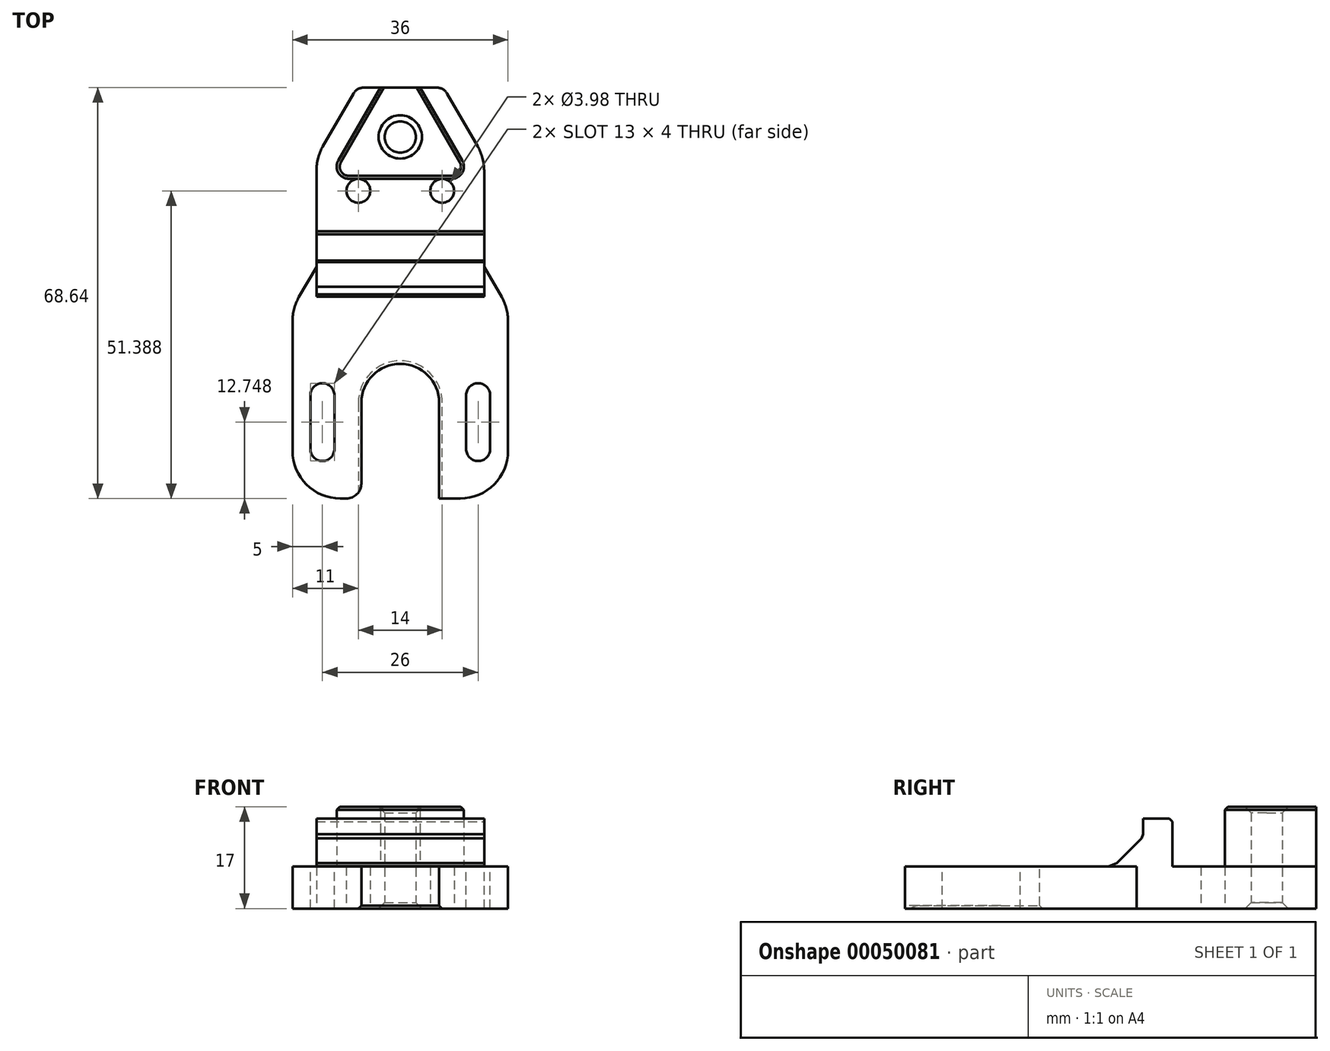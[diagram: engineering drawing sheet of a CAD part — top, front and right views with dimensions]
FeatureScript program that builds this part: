
annotation { "Feature Type Name" : "Feature", "Feature Type Description" : "" }
export const myFeature = defineFeature(function(context is Context, id is Id, definition is map)
    precondition{}
    {
        {
            var Q0;
            Q0=qCreatedBy(makeId("Top.planeOp"),FACE);
            var sketch = newSketch(context, id + "F0", { "sketchPlane" : qUnion([Q0])});
            skLineSegment(sketch, "E0", {"start": v(-12.34, -7.12) * mm, "end": v(0, 14.25) * mm});
            skLineSegment(sketch, "E1", {"start": v(0, 14.25) * mm, "end": v(12.34, -7.12) * mm});
            skLineSegment(sketch, "E2", {"start": v(12.34, -7.12) * mm, "end": v(-12.34, -7.12) * mm});
            skLineSegment(sketch, "E3", {"start": v(-12.34, -7.12) * mm, "end": v(6.17, 3.56) * mm, "construction": true});
            skPoint(sketch, "E3.endSnap0", {"position": v(6.17, 3.56) * mm});
            skLineSegment(sketch, "E4", {"start": v(12.34, -7.12) * mm, "end": v(-6.17, 3.56) * mm, "construction": true});
            skPoint(sketch, "E5", {"position": v(0, 0) * mm});
            skSolve(sketch);
        }
        {
            var Q0;
            Q0 = qSketchRegion(id + "F0", true);
            extrude(context, id + "F1", {"entities" : qUnion([Q0]), "depth" : 10 * mm, "offsetDistance" : 25 * mm});
        }
        {
            var Q0;
            Q0=makeQuery(id+"F1.opExtrude","CAP_FACE",FACE,{"disambiguationData":[OSD([sQuery(id+"F0.wireOp",EDGE,"E0"),sQuery(id+"F0.wireOp",EDGE,"E1"),sQuery(id+"F0.wireOp",EDGE,"E2")])],"isStart":true});
            var sketch = newSketch(context, id + "F2", { "sketchPlane" : qUnion([Q0])});
            skLineSegment(sketch, "E6", {"start": v(0, -20.78) * mm, "end": v(-18, 10.4) * mm});
            skLineSegment(sketch, "E7", {"start": v(-18, 10.4) * mm, "end": v(18, 10.4) * mm});
            skLineSegment(sketch, "E8", {"start": v(18, 10.4) * mm, "end": v(0, -20.78) * mm});
            skLineSegment(sketch, "E9", {"start": v(18, 10.4) * mm, "end": v(-9, -5.2) * mm, "construction": true});
            skLineSegment(sketch, "E10", {"start": v(0, -20.78) * mm, "end": v(0, 10.4) * mm, "construction": true});
            skLineSegment(sketch, "E11", {"start": v(-18, 10.4) * mm, "end": v(9, -5.2) * mm, "construction": true});
            skPoint(sketch, "E12", {"position": v(0, 0) * mm});
            skSolve(sketch);
        }
        {
            var Q0;
            Q0 = qSketchRegion(id + "F2", true);
            extrude(context, id + "F3", {"entities" : qUnion([Q0]), "operationType" : NewBodyOperationType.ADD, "depth" : 7 * mm, "offsetDistance" : 25 * mm});
        }
        {
            var Q0;
            Q0=qCreatedBy(makeId("Top.planeOp"),FACE);
            var sketch = newSketch(context, id + "F4", { "sketchPlane" : qUnion([Q0])});
            skLineSegment(sketch, "E13.0", {"start": v(-18, -10.4) * mm, "end": v(18, -10.4) * mm, "construction": true});
            skPoint(sketch, "E14.0", {"position": v(0, 14.25) * mm});
            skLineSegment(sketch, "E15", {"start": v(-11.46, 8.25) * mm, "end": v(13.33, 8.25) * mm});
            skLineSegment(sketch, "E16", {"start": v(13.33, 8.25) * mm, "end": v(13.33, 20.97) * mm});
            skLineSegment(sketch, "E17", {"start": v(13.33, 20.97) * mm, "end": v(-11.55, 20.97) * mm});
            skLineSegment(sketch, "E18", {"start": v(-11.55, 20.97) * mm, "end": v(-11.46, 8.25) * mm});
            skLineSegment(sketch, "E19.0", {"start": v(0, 20.78) * mm, "end": v(-18, -10.4) * mm, "construction": true});
            skLineSegment(sketch, "E20.0", {"start": v(18, -10.4) * mm, "end": v(0, 20.78) * mm, "construction": true});
            skLineSegment(sketch, "E21", {"start": v(-18, -10.4) * mm, "end": v(9, 5.2) * mm, "construction": true});
            skLineSegment(sketch, "E22", {"start": v(18, -10.4) * mm, "end": v(-9, 5.2) * mm, "construction": true});
            skPoint(sketch, "E23", {"position": v(0, 0) * mm});
            skCircle(sketch, "E24", {"center": v(0, 0) * mm, "radius": 2.62 * mm});
            skLineSegment(sketch, "E25.bottom", {"start": v(-19, -3) * mm, "end": v(-14, -3) * mm});
            skLineSegment(sketch, "E25.top", {"start": v(-19, -13) * mm, "end": v(-14, -13) * mm});
            skLineSegment(sketch, "E25.left", {"start": v(-19, -3) * mm, "end": v(-19, -13) * mm});
            skLineSegment(sketch, "E25.right", {"start": v(-14, -3) * mm, "end": v(-14, -13) * mm});
            skLineSegment(sketch, "E26.MirrorCS", {"start": v(19, -13) * mm, "end": v(14, -13) * mm});
            skLineSegment(sketch, "E27.MirrorCS", {"start": v(14, -3) * mm, "end": v(14, -13) * mm});
            skLineSegment(sketch, "E28.MirrorCS", {"start": v(19, -3) * mm, "end": v(19, -13) * mm});
            skLineSegment(sketch, "E29.MirrorCS", {"start": v(19, -3) * mm, "end": v(14, -3) * mm});
            skSolve(sketch);
        }
        {
            var Q0;
            Q0 = qSketchRegion(id + "F4", true);
            extrude(context, id + "F5", {"entities" : qUnion([Q0]), "operationType" : NewBodyOperationType.REMOVE, "endBound" : BoundingType.THROUGH_ALL, "depth" : 25 * mm, "hasSecondDirection" : true, "secondDirectionOppositeDirection" : true, "secondDirectionDepth" : 25 * mm, "offsetDistance" : 25 * mm});
        }
        {
            var Q0;
            Q0=makeQuery(id+"F3.opExtrude","SWEPT_FACE",FACE,{"disambiguationData":[OSD([sQuery(id+"F2.wireOp",EDGE,"E7")])]});
            var sketch = newSketch(context, id + "F6", { "sketchPlane" : qUnion([Q0])});
            skLineSegment(sketch, "E30.0", {"start": v(-14, -7) * mm, "end": v(-14, 0) * mm});
            skLineSegment(sketch, "E30.1", {"start": v(-14, -7) * mm, "end": v(14, -7) * mm});
            skLineSegment(sketch, "E30.2", {"start": v(14, -7) * mm, "end": v(14, 0) * mm});
            skLineSegment(sketch, "E30.3", {"start": v(-14, 0) * mm, "end": v(14, 0) * mm});
            skSolve(sketch);
        }
        {
            var Q0;
            Q0 = qSketchRegion(id + "F6", true);
            extrude(context, id + "F7", {"entities" : qUnion([Q0]), "operationType" : NewBodyOperationType.ADD, "depth" : 50 * mm, "offsetDistance" : 25 * mm});
        }
        {
            var Q0;
            Q0=makeQuery(id+"F7.boolean.opBoolean","MERGE",FACE,{"derivedFrom":[makeQuery(id+"F3.opExtrude","CAP_FACE",FACE,{"disambiguationData":[OSD([sQuery(id+"F2.wireOp",EDGE,"E6"),sQuery(id+"F2.wireOp",EDGE,"E7"),sQuery(id+"F2.wireOp",EDGE,"E8")])],"isStart":true}),makeQuery(id+"F7.opExtrude","SWEPT_FACE",FACE,{"disambiguationData":[OSD([sQuery(id+"F6.wireOp",EDGE,"E30.3")])]})]});
            var sketch = newSketch(context, id + "F8", { "sketchPlane" : qUnion([Q0])});
            skLineSegment(sketch, "E31.bottom", {"start": v(-14, -15.62) * mm, "end": v(14, -15.62) * mm});
            skLineSegment(sketch, "E31.top", {"start": v(-14, -20.62) * mm, "end": v(14, -20.62) * mm});
            skLineSegment(sketch, "E31.left", {"start": v(-14, -15.62) * mm, "end": v(-14, -20.62) * mm});
            skLineSegment(sketch, "E31.right", {"start": v(14, -15.62) * mm, "end": v(14, -20.62) * mm});
            skSolve(sketch);
        }
        {
            var Q0;
            Q0 = qSketchRegion(id + "F8", true);
            extrude(context, id + "F9", {"entities" : qUnion([Q0]), "operationType" : NewBodyOperationType.ADD, "depth" : 8 * mm});
        }
        {
            var Q0;
            Q0=makeQuery(id+"F9.opExtrude","CAP_EDGE",EDGE,{"disambiguationData":[OSD([sQuery(id+"F8.wireOp",EDGE,"E31.top")])],"isStart":true});
            chamfer(context, id + "F10", {"entities" : qUnion([Q0]), "width" : 5 * mm, "tangentPropagation" : true});
        }
        {
            var Q0;
            {var subQ1=sQuery(id+"F6.wireOp",EDGE,"E30.3");var subQ3=sQuery(id+"F8.wireOp",EDGE,"E31.top");Q0=makeQuery(id+"F10.opChamfer","BLEND_EDGE",EDGE,{"blendedFrom":[makeQuery(id+"F9.opExtrude","CAP_EDGE",EDGE,{"disambiguationData":[OSD([subQ3])],"isStart":true}),makeQuery(id+"F9.boolean.opBoolean","SPLIT",FACE,{"disambiguationData":[TD([makeQuery(id+"F9.opExtrude","SWEPT_FACE",FACE,{"disambiguationData":[OSD([subQ3])]})])],"derivedFrom":makeQuery(id+"F7.boolean.opBoolean","MERGE",FACE,{"derivedFrom":[makeQuery(id+"F3.opExtrude","CAP_FACE",FACE,{"disambiguationData":[OSD([sQuery(id+"F2.wireOp",EDGE,"E6"),sQuery(id+"F2.wireOp",EDGE,"E7"),sQuery(id+"F2.wireOp",EDGE,"E8")])],"isStart":true}),makeQuery(id+"F7.opExtrude","SWEPT_FACE",FACE,{"disambiguationData":[OSD([subQ1])]})]})})],"blendedInto":[makeQuery(id+"F9.boolean.opBoolean","SPLIT",FACE,{"disambiguationData":[TD([makeQuery(id+"F9.opExtrude","SWEPT_FACE",FACE,{"disambiguationData":[OSD([subQ3])]})])],"derivedFrom":makeQuery(id+"F7.boolean.opBoolean","MERGE",FACE,{"derivedFrom":[makeQuery(id+"F3.opExtrude","CAP_FACE",FACE,{"disambiguationData":[OSD([sQuery(id+"F2.wireOp",EDGE,"E6"),sQuery(id+"F2.wireOp",EDGE,"E7"),sQuery(id+"F2.wireOp",EDGE,"E8")])],"isStart":true}),makeQuery(id+"F7.opExtrude","SWEPT_FACE",FACE,{"disambiguationData":[OSD([subQ1])]})]})})]});}
            chamfer(context, id + "F11", {"entities" : qUnion([Q0]), "width" : 2 * mm, "tangentPropagation" : true});
        }
        {
            var Q0;
            {var subQ1=sQuery(id+"F6.wireOp",EDGE,"E30.3");var subQ3=sQuery(id+"F8.wireOp",EDGE,"E31.top");var subQ4=makeQuery(id+"F9.boolean.opBoolean","SPLIT",FACE,{"disambiguationData":[TD([makeQuery(id+"F9.opExtrude","SWEPT_FACE",FACE,{"disambiguationData":[OSD([subQ3])]})])],"derivedFrom":makeQuery(id+"F7.boolean.opBoolean","MERGE",FACE,{"derivedFrom":[makeQuery(id+"F3.opExtrude","CAP_FACE",FACE,{"disambiguationData":[OSD([sQuery(id+"F2.wireOp",EDGE,"E6"),sQuery(id+"F2.wireOp",EDGE,"E7"),sQuery(id+"F2.wireOp",EDGE,"E8")])],"isStart":true}),makeQuery(id+"F7.opExtrude","SWEPT_FACE",FACE,{"disambiguationData":[OSD([subQ1])]})]})});Q0=makeQuery(id+"F11.opChamfer","BLEND_EDGE",EDGE,{"blendedFrom":[makeQuery(id+"F10.opChamfer","BLEND_EDGE",EDGE,{"blendedFrom":[makeQuery(id+"F9.opExtrude","CAP_EDGE",EDGE,{"disambiguationData":[OSD([subQ3])],"isStart":true}),subQ4],"blendedInto":[subQ4]}),subQ4],"blendedInto":[subQ4]});}
            chamfer(context, id + "F12", {"entities" : qUnion([Q0]), "width" : 1 * mm, "tangentPropagation" : true});
        }
        {
            var Q0;
            {var subQ0=sQuery(id+"F8.wireOp",EDGE,"E31.top");Q0=makeQuery(id+"F10.opChamfer","BLEND_EDGE",EDGE,{"blendedFrom":[makeQuery(id+"F9.opExtrude","CAP_EDGE",EDGE,{"disambiguationData":[OSD([subQ0])],"isStart":true}),makeQuery(id+"F9.opExtrude","SWEPT_FACE",FACE,{"disambiguationData":[OSD([subQ0])]})],"blendedInto":[makeQuery(id+"F9.opExtrude","SWEPT_FACE",FACE,{"disambiguationData":[OSD([subQ0])]})]});}
            chamfer(context, id + "F13", {"entities" : qUnion([Q0]), "width" : 1 * mm, "tangentPropagation" : true});
        }
        {
            var Q0;
            Q0=makeQuery(id+"F5.boolean.opBoolean","INTERSECT",EDGE,{"derivedFrom":[makeQuery(id+"F3.opExtrude","SWEPT_FACE",FACE,{"disambiguationData":[OSD([sQuery(id+"F2.wireOp",EDGE,"E6")])]}),makeQuery(id+"F5.opExtrude","SWEPT_FACE",FACE,{"disambiguationData":[OSD([sQuery(id+"F4.wireOp",EDGE,"E25.right")])]})]});
            var Q1;
            Q1=makeQuery(id+"F5.boolean.opBoolean","INTERSECT",EDGE,{"derivedFrom":[makeQuery(id+"F3.opExtrude","SWEPT_FACE",FACE,{"disambiguationData":[OSD([sQuery(id+"F2.wireOp",EDGE,"E8")])]}),makeQuery(id+"F5.opExtrude","SWEPT_FACE",FACE,{"disambiguationData":[OSD([sQuery(id+"F4.wireOp",EDGE,"E27.MirrorCS")])]})]});
            fillet(context, id + "F14", {"entities" : qUnion([Q0, Q1]), "radius" : 8 * mm, "tangentPropagation" : true, "allowEdgeOverflow" : false});
        }
        {
            var Q0;
            Q0=makeQuery(id+"F5.boolean.opBoolean","INTERSECT",EDGE,{"derivedFrom":[makeQuery(id+"F1.opExtrude","CAP_FACE",FACE,{"disambiguationData":[OSD([sQuery(id+"F0.wireOp",EDGE,"E0"),sQuery(id+"F0.wireOp",EDGE,"E1"),sQuery(id+"F0.wireOp",EDGE,"E2")])],"isStart":false}),makeQuery(id+"F5.opExtrude","SWEPT_FACE",FACE,{"disambiguationData":[OSD([sQuery(id+"F4.wireOp",EDGE,"E24")])]})]});
            var Q1;
            Q1=makeQuery(id+"F5.boolean.opBoolean","INTERSECT",EDGE,{"derivedFrom":[makeQuery(id+"F3.opExtrude","CAP_FACE",FACE,{"disambiguationData":[OSD([sQuery(id+"F2.wireOp",EDGE,"E6"),sQuery(id+"F2.wireOp",EDGE,"E7"),sQuery(id+"F2.wireOp",EDGE,"E8")])],"isStart":false}),makeQuery(id+"F5.opExtrude","SWEPT_FACE",FACE,{"disambiguationData":[OSD([sQuery(id+"F4.wireOp",EDGE,"E24")])]})]});
            chamfer(context, id + "F15", {"entities" : qUnion([Q0, Q1]), "width" : 1 * mm, "tangentPropagation" : true});
        }
        {
            var Q0;
            {var subQ0=sQuery(id+"F2.wireOp",EDGE,"E8");var subQ1=sQuery(id+"F2.wireOp",EDGE,"E6");Q0=makeQuery(id+"F9.boolean.opBoolean","SPLIT",FACE,{"disambiguationData":[TD([makeQuery(id+"F1.opExtrude","SWEPT_FACE",FACE,{"disambiguationData":[OSD([sQuery(id+"F0.wireOp",EDGE,"E0")])]})])],"derivedFrom":makeQuery(id+"F7.boolean.opBoolean","MERGE",FACE,{"derivedFrom":[makeQuery(id+"F3.opExtrude","CAP_FACE",FACE,{"disambiguationData":[OSD([subQ1,sQuery(id+"F2.wireOp",EDGE,"E7"),subQ0])],"isStart":true}),makeQuery(id+"F7.opExtrude","SWEPT_FACE",FACE,{"disambiguationData":[OSD([sQuery(id+"F6.wireOp",EDGE,"E30.3")])]})]})});}
            var sketch = newSketch(context, id + "F16", { "sketchPlane" : qUnion([Q0])});
            skLineSegment(sketch, "E32.0", {"start": v(-12.08, -6.97) * mm, "end": v(-3.3, 8.25) * mm});
            skLineSegment(sketch, "E32.1", {"start": v(12.08, -6.97) * mm, "end": v(-12.08, -6.97) * mm});
            skLineSegment(sketch, "E32.2", {"start": v(3.3, 8.25) * mm, "end": v(12.08, -6.97) * mm});
            skLineSegment(sketch, "E33.0", {"start": v(-14, -15.77) * mm, "end": v(14, -15.77) * mm});
            skLineSegment(sketch, "E34", {"start": v(-14, -15.77) * mm, "end": v(-14, 8.25) * mm});
            skPoint(sketch, "E34.endSnap0", {"position": v(-14, -10.62) * mm});
            skLineSegment(sketch, "E35", {"start": v(14, -15.77) * mm, "end": v(14, 8.25) * mm});
            skLineSegment(sketch, "E36", {"start": v(7.24, 8.25) * mm, "end": v(3.3, 8.25) * mm});
            skLineSegment(sketch, "E37", {"start": v(7.24, 8.25) * mm, "end": v(14, 8.25) * mm});
            skLineSegment(sketch, "E38.trimOffspring", {"start": v(-3.3, 8.25) * mm, "end": v(-14, 8.25) * mm});
            skSolve(sketch);
        }
        {
            var Q0;
            Q0 = qSketchRegion(id + "F16", true);
            extrude(context, id + "F17", {"entities" : qUnion([Q0]), "operationType" : NewBodyOperationType.REMOVE, "endBound" : BoundingType.THROUGH_ALL, "depth" : 25 * mm});
        }
        {
            var Q0;
            Q0=makeQuery(id+"F17.boolean.opBoolean","COPY",EDGE,{"derivedFrom":makeQuery(id+"F17.opExtrude","SWEPT_EDGE",EDGE,{"disambiguationData":[OSD([sQuery(id+"F16.wireOp",EDGE,"E32.0"),sQuery(id+"F16.wireOp",EDGE,"E32.1")])]})});
            var Q1;
            Q1=makeQuery(id+"F17.boolean.opBoolean","COPY",EDGE,{"derivedFrom":makeQuery(id+"F17.opExtrude","SWEPT_EDGE",EDGE,{"disambiguationData":[OSD([sQuery(id+"F16.wireOp",EDGE,"E32.1"),sQuery(id+"F16.wireOp",EDGE,"E32.2")])]})});
            var Q2;
            Q2=makeQuery(id+"F17.boolean.opBoolean","COPY",EDGE,{"derivedFrom":makeQuery(id+"F17.opExtrude","SWEPT_EDGE",EDGE,{"disambiguationData":[OSD([sQuery(id+"F16.wireOp",EDGE,"E32.2"),sQuery(id+"F16.wireOp",EDGE,"E36")])]})});
            var Q3;
            Q3=makeQuery(id+"F17.boolean.opBoolean","COPY",EDGE,{"derivedFrom":makeQuery(id+"F17.opExtrude","SWEPT_EDGE",EDGE,{"disambiguationData":[OSD([sQuery(id+"F16.wireOp",EDGE,"E32.0"),sQuery(id+"F16.wireOp",EDGE,"E38.trimOffspring")])]})});
            var Q4;
            Q4=makeQuery(id+"F5.boolean.opBoolean","INTERSECT",EDGE,{"derivedFrom":[makeQuery(id+"F3.opExtrude","SWEPT_FACE",FACE,{"disambiguationData":[OSD([sQuery(id+"F2.wireOp",EDGE,"E6")])]}),makeQuery(id+"F5.opExtrude","SWEPT_FACE",FACE,{"disambiguationData":[OSD([sQuery(id+"F4.wireOp",EDGE,"E15")])]})]});
            var Q5;
            Q5=makeQuery(id+"F5.boolean.opBoolean","INTERSECT",EDGE,{"derivedFrom":[makeQuery(id+"F3.opExtrude","SWEPT_FACE",FACE,{"disambiguationData":[OSD([sQuery(id+"F2.wireOp",EDGE,"E8")])]}),makeQuery(id+"F5.opExtrude","SWEPT_FACE",FACE,{"disambiguationData":[OSD([sQuery(id+"F4.wireOp",EDGE,"E15")])]})]});
            var Q6;
            Q6=makeQuery(id+"F17.boolean.opBoolean","COPY",EDGE,{"derivedFrom":makeQuery(id+"F17.opExtrude","SWEPT_EDGE",EDGE,{"disambiguationData":[OSD([sQuery(id+"F16.wireOp",EDGE,"E33.0"),sQuery(id+"F16.wireOp",EDGE,"E34")])]})});
            var Q7;
            Q7=makeQuery(id+"F17.boolean.opBoolean","COPY",EDGE,{"derivedFrom":makeQuery(id+"F17.opExtrude","SWEPT_EDGE",EDGE,{"disambiguationData":[OSD([sQuery(id+"F16.wireOp",EDGE,"E33.0"),sQuery(id+"F16.wireOp",EDGE,"E35")])]})});
            fillet(context, id + "F18", {"entities" : qUnion([Q0, Q1, Q2, Q3, Q4, Q5, Q6, Q7]), "radius" : 2 * mm, "tangentPropagation" : true, "allowEdgeOverflow" : false});
        }
        {
            var Q0;
            {var subQ1=sQuery(id+"F6.wireOp",EDGE,"E30.3");Q0=makeQuery(id+"F9.boolean.opBoolean","SPLIT",FACE,{"disambiguationData":[TD([makeQuery(id+"F9.opExtrude","SWEPT_FACE",FACE,{"disambiguationData":[OSD([sQuery(id+"F8.wireOp",EDGE,"E31.top")])]})])],"derivedFrom":makeQuery(id+"F7.boolean.opBoolean","MERGE",FACE,{"derivedFrom":[makeQuery(id+"F3.opExtrude","CAP_FACE",FACE,{"disambiguationData":[OSD([sQuery(id+"F2.wireOp",EDGE,"E6"),sQuery(id+"F2.wireOp",EDGE,"E7"),sQuery(id+"F2.wireOp",EDGE,"E8")])],"isStart":true}),makeQuery(id+"F7.opExtrude","SWEPT_FACE",FACE,{"disambiguationData":[OSD([subQ1])]})]})});}
            var sketch = newSketch(context, id + "F19", { "sketchPlane" : qUnion([Q0])});
            skLineSegment(sketch, "E39", {"start": v(0, -60.4) * mm, "end": v(0, -44.4) * mm, "construction": true});
            skPoint(sketch, "E39.endSnap0", {"position": v(0, -60.4) * mm});
            skArc(sketch, "E40", {"start": v(6.5, -44.4) * mm, "mid": v(0, -37.9) * mm, "end": v(-6.5, -44.4) * mm});
            skLineSegment(sketch, "E41", {"start": v(6.5, -50.9) * mm, "end": v(6.5, -44.4) * mm});
            skLineSegment(sketch, "E42", {"start": v(-6.5, -44.4) * mm, "end": v(-6.5, -50.9) * mm});
            skLineSegment(sketch, "E43", {"start": v(-6.5, -50.9) * mm, "end": v(-6.5, -60.4) * mm});
            skLineSegment(sketch, "E44", {"start": v(6.5, -50.9) * mm, "end": v(6.5, -60.4) * mm});
            skLineSegment(sketch, "E45", {"start": v(6.5, -60.4) * mm, "end": v(-6.5, -60.4) * mm});
            skPoint(sketch, "E46.center.orphan", {"position": v(0, -50.9) * mm});
            skSolve(sketch);
        }
        {
            var Q0;
            Q0 = qSketchRegion(id + "F19", true);
            extrude(context, id + "F20", {"entities" : qUnion([Q0]), "operationType" : NewBodyOperationType.REMOVE, "endBound" : BoundingType.THROUGH_ALL, "oppositeDirection" : true, "depth" : 25 * mm});
        }
        {
            var Q0;
            {var subQ1=sQuery(id+"F6.wireOp",EDGE,"E30.3");Q0=makeQuery(id+"F9.boolean.opBoolean","SPLIT",FACE,{"disambiguationData":[TD([makeQuery(id+"F9.opExtrude","SWEPT_FACE",FACE,{"disambiguationData":[OSD([sQuery(id+"F8.wireOp",EDGE,"E31.top")])]})])],"derivedFrom":makeQuery(id+"F7.boolean.opBoolean","MERGE",FACE,{"derivedFrom":[makeQuery(id+"F3.opExtrude","CAP_FACE",FACE,{"disambiguationData":[OSD([sQuery(id+"F2.wireOp",EDGE,"E6"),sQuery(id+"F2.wireOp",EDGE,"E7"),sQuery(id+"F2.wireOp",EDGE,"E8")])],"isStart":true}),makeQuery(id+"F7.opExtrude","SWEPT_FACE",FACE,{"disambiguationData":[OSD([subQ1])]})]})});}
            var sketch = newSketch(context, id + "F21", { "sketchPlane" : qUnion([Q0])});
            skLineSegment(sketch, "E47.0", {"start": v(-14, -28.62) * mm, "end": v(-14, -60.4) * mm});
            skLineSegment(sketch, "E48", {"start": v(-14, -60.4) * mm, "end": v(-18, -60.4) * mm});
            skLineSegment(sketch, "E49", {"start": v(-18, -60.4) * mm, "end": v(-18, -28.62) * mm});
            skLineSegment(sketch, "E50", {"start": v(-18, -28.62) * mm, "end": v(-14, -21.7) * mm});
            skLineSegment(sketch, "E51", {"start": v(-14, -21.7) * mm, "end": v(-14, -28.62) * mm});
            skLineSegment(sketch, "E52.MirrorCS", {"start": v(14, -60.4) * mm, "end": v(18, -60.4) * mm});
            skLineSegment(sketch, "E53.MirrorCS", {"start": v(18, -60.4) * mm, "end": v(18, -28.62) * mm});
            skLineSegment(sketch, "E54.MirrorCS", {"start": v(14, -28.62) * mm, "end": v(14, -60.4) * mm});
            skLineSegment(sketch, "E55.MirrorCS", {"start": v(18, -28.62) * mm, "end": v(14, -21.7) * mm});
            skLineSegment(sketch, "E56.MirrorCS", {"start": v(14, -21.7) * mm, "end": v(14, -28.62) * mm});
            skSolve(sketch);
        }
        {
            var Q0;
            Q0 = qSketchRegion(id + "F21", true);
            var Q1;
            Q1=makeQuery(id+"F7.boolean.opBoolean","MERGE",FACE,{"derivedFrom":[makeQuery(id+"F3.opExtrude","CAP_FACE",FACE,{"disambiguationData":[OSD([sQuery(id+"F2.wireOp",EDGE,"E6"),sQuery(id+"F2.wireOp",EDGE,"E7"),sQuery(id+"F2.wireOp",EDGE,"E8")])],"isStart":false}),makeQuery(id+"F7.opExtrude","SWEPT_FACE",FACE,{"disambiguationData":[OSD([sQuery(id+"F6.wireOp",EDGE,"E30.1")])]})]});
            extrude(context, id + "F22", {"entities" : qUnion([Q0]), "operationType" : NewBodyOperationType.ADD, "endBound" : BoundingType.UP_TO_SURFACE, "oppositeDirection" : true, "endBoundEntityFace" : qUnion([Q1]), "depth" : 25 * mm});
        }
        {
            var Q0;
            Q0=makeQuery(id+"F22.opExtrude","SWEPT_EDGE",EDGE,{"disambiguationData":[OSD([sQuery(id+"F21.wireOp",EDGE,"E53.MirrorCS"),sQuery(id+"F21.wireOp",EDGE,"E55.MirrorCS")])]});
            var Q1;
            Q1=makeQuery(id+"F22.opExtrude","SWEPT_EDGE",EDGE,{"disambiguationData":[OSD([sQuery(id+"F21.wireOp",EDGE,"E55.MirrorCS"),sQuery(id+"F21.wireOp",EDGE,"E56.MirrorCS")])]});
            var Q2;
            Q2=makeQuery(id+"F22.opExtrude","SWEPT_EDGE",EDGE,{"disambiguationData":[OSD([sQuery(id+"F21.wireOp",EDGE,"E50"),sQuery(id+"F21.wireOp",EDGE,"E51")])]});
            var Q3;
            Q3=makeQuery(id+"F22.opExtrude","SWEPT_EDGE",EDGE,{"disambiguationData":[OSD([sQuery(id+"F21.wireOp",EDGE,"E49"),sQuery(id+"F21.wireOp",EDGE,"E50")])]});
            var Q4;
            Q4=makeQuery(id+"F22.opExtrude","SWEPT_EDGE",EDGE,{"disambiguationData":[OSD([sQuery(id+"F21.wireOp",EDGE,"E48"),sQuery(id+"F21.wireOp",EDGE,"E49")])]});
            var Q5;
            Q5=makeQuery(id+"F22.opExtrude","SWEPT_EDGE",EDGE,{"disambiguationData":[OSD([sQuery(id+"F21.wireOp",EDGE,"E52.MirrorCS"),sQuery(id+"F21.wireOp",EDGE,"E53.MirrorCS")])]});
            fillet(context, id + "F23", {"entities" : qUnion([Q0, Q1, Q2, Q3, Q4, Q5]), "radius" : 8 * mm, "tangentPropagation" : true, "allowEdgeOverflow" : false});
        }
        {
            var Q0;
            {var subQ1=sQuery(id+"F6.wireOp",EDGE,"E30.3");Q0=makeQuery(id+"F9.boolean.opBoolean","SPLIT",FACE,{"disambiguationData":[TD([makeQuery(id+"F9.opExtrude","SWEPT_FACE",FACE,{"disambiguationData":[OSD([sQuery(id+"F8.wireOp",EDGE,"E31.top")])]})])],"derivedFrom":makeQuery(id+"F7.boolean.opBoolean","MERGE",FACE,{"derivedFrom":[makeQuery(id+"F3.opExtrude","CAP_FACE",FACE,{"disambiguationData":[OSD([sQuery(id+"F2.wireOp",EDGE,"E6"),sQuery(id+"F2.wireOp",EDGE,"E7"),sQuery(id+"F2.wireOp",EDGE,"E8")])],"isStart":true}),makeQuery(id+"F7.opExtrude","SWEPT_FACE",FACE,{"disambiguationData":[OSD([subQ1])]})]})});}
            var sketch = newSketch(context, id + "F24", { "sketchPlane" : qUnion([Q0])});
            skLineSegment(sketch, "E57", {"start": v(0, -44.4) * mm, "end": v(-13, -44.4) * mm, "construction": true});
            skLineSegment(sketch, "E58", {"start": v(-13, -44.4) * mm, "end": v(-13, -50.9) * mm, "construction": true});
            skArc(sketch, "E59.0", {"start": v(6.5, -44.4) * mm, "mid": v(0, -37.9) * mm, "end": v(-6.5, -44.4) * mm, "construction": true});
            skArc(sketch, "E60.0", {"start": v(-6.5, -50.9) * mm, "mid": v(0, -57.4) * mm, "end": v(6.5, -50.9) * mm, "construction": true});
            skLineSegment(sketch, "E61", {"start": v(-13, -44.4) * mm, "end": v(-13, -43.14) * mm, "construction": true});
            skLineSegment(sketch, "E62", {"start": v(-13, -50.9) * mm, "end": v(-13, -52.14) * mm, "construction": true});
            skArc(sketch, "E63", {"start": v(-11, -43.14) * mm, "mid": v(-13, -41.14) * mm, "end": v(-15, -43.14) * mm});
            skArc(sketch, "E64", {"start": v(-15, -52.14) * mm, "mid": v(-13, -54.14) * mm, "end": v(-11, -52.14) * mm});
            skLineSegment(sketch, "E65", {"start": v(-11, -43.14) * mm, "end": v(-11, -52.14) * mm});
            skLineSegment(sketch, "E66", {"start": v(-15, -43.14) * mm, "end": v(-15, -52.14) * mm});
            skLineSegment(sketch, "E67.MirrorCS", {"start": v(15, -43.14) * mm, "end": v(15, -52.14) * mm});
            skLineSegment(sketch, "E68.MirrorCS", {"start": v(11, -43.14) * mm, "end": v(11, -52.14) * mm});
            skArc(sketch, "E69.MirrorCS", {"start": v(15, -52.14) * mm, "mid": v(13, -54.14) * mm, "end": v(11, -52.14) * mm});
            skArc(sketch, "E70.MirrorCS", {"start": v(11, -43.14) * mm, "mid": v(13, -41.14) * mm, "end": v(15, -43.14) * mm});
            skSolve(sketch);
        }
        {
            var Q0;
            Q0 = qSketchRegion(id + "F24", true);
            extrude(context, id + "F25", {"entities" : qUnion([Q0]), "operationType" : NewBodyOperationType.REMOVE, "endBound" : BoundingType.THROUGH_ALL, "oppositeDirection" : true, "depth" : 25 * mm});
        }
        {
            var Q0;
            Q0=makeQuery(id+"F25.boolean.opBoolean","INTERSECT",EDGE,{"derivedFrom":[makeQuery(id+"F22.boolean.opBoolean","MERGE",FACE,{"derivedFrom":[makeQuery(id+"F7.boolean.opBoolean","MERGE",FACE,{"derivedFrom":[makeQuery(id+"F3.opExtrude","CAP_FACE",FACE,{"disambiguationData":[OSD([sQuery(id+"F2.wireOp",EDGE,"E6"),sQuery(id+"F2.wireOp",EDGE,"E7"),sQuery(id+"F2.wireOp",EDGE,"E8")])],"isStart":false}),makeQuery(id+"F7.opExtrude","SWEPT_FACE",FACE,{"disambiguationData":[OSD([sQuery(id+"F6.wireOp",EDGE,"E30.1")])]})]}),makeQuery(id+"F22.opExtrude","CAP_FACE",FACE,{"disambiguationData":[OSD([sQuery(id+"F21.wireOp",EDGE,"E47.0"),sQuery(id+"F21.wireOp",EDGE,"E48"),sQuery(id+"F21.wireOp",EDGE,"E49"),sQuery(id+"F21.wireOp",EDGE,"E50"),sQuery(id+"F21.wireOp",EDGE,"E51")])],"isStart":false}),makeQuery(id+"F22.opExtrude","CAP_FACE",FACE,{"disambiguationData":[OSD([sQuery(id+"F21.wireOp",EDGE,"E52.MirrorCS"),sQuery(id+"F21.wireOp",EDGE,"E53.MirrorCS"),sQuery(id+"F21.wireOp",EDGE,"E54.MirrorCS"),sQuery(id+"F21.wireOp",EDGE,"E55.MirrorCS"),sQuery(id+"F21.wireOp",EDGE,"E56.MirrorCS")])],"isStart":false})]}),makeQuery(id+"F25.opExtrude","SWEPT_FACE",FACE,{"disambiguationData":[OSD([sQuery(id+"F24.wireOp",EDGE,"UyVIg1no-6ILB-DUvu-GGRX-9YdGvvApEaQs")])]})]});
            var Q1;
            Q1=makeQuery(id+"F25.boolean.opBoolean","INTERSECT",EDGE,{"derivedFrom":[makeQuery(id+"F22.boolean.opBoolean","MERGE",FACE,{"derivedFrom":[makeQuery(id+"F7.boolean.opBoolean","MERGE",FACE,{"derivedFrom":[makeQuery(id+"F3.opExtrude","CAP_FACE",FACE,{"disambiguationData":[OSD([sQuery(id+"F2.wireOp",EDGE,"E6"),sQuery(id+"F2.wireOp",EDGE,"E7"),sQuery(id+"F2.wireOp",EDGE,"E8")])],"isStart":false}),makeQuery(id+"F7.opExtrude","SWEPT_FACE",FACE,{"disambiguationData":[OSD([sQuery(id+"F6.wireOp",EDGE,"E30.1")])]})]}),makeQuery(id+"F22.opExtrude","CAP_FACE",FACE,{"disambiguationData":[OSD([sQuery(id+"F21.wireOp",EDGE,"E47.0"),sQuery(id+"F21.wireOp",EDGE,"E48"),sQuery(id+"F21.wireOp",EDGE,"E49"),sQuery(id+"F21.wireOp",EDGE,"E50"),sQuery(id+"F21.wireOp",EDGE,"E51")])],"isStart":false}),makeQuery(id+"F22.opExtrude","CAP_FACE",FACE,{"disambiguationData":[OSD([sQuery(id+"F21.wireOp",EDGE,"E52.MirrorCS"),sQuery(id+"F21.wireOp",EDGE,"E53.MirrorCS"),sQuery(id+"F21.wireOp",EDGE,"E54.MirrorCS"),sQuery(id+"F21.wireOp",EDGE,"E55.MirrorCS"),sQuery(id+"F21.wireOp",EDGE,"E56.MirrorCS")])],"isStart":false})]}),makeQuery(id+"F25.opExtrude","SWEPT_FACE",FACE,{"disambiguationData":[OSD([sQuery(id+"F24.wireOp",EDGE,"746c9b08-4bf7-42f0-bad6-eb23918db56c3.MirrorCS")])]})]});
            var Q2;
            Q2=makeQuery(id+"F20.boolean.opBoolean","INTERSECT",EDGE,{"derivedFrom":[makeQuery(id+"F7.boolean.opBoolean","MERGE",FACE,{"derivedFrom":[makeQuery(id+"F3.opExtrude","CAP_FACE",FACE,{"disambiguationData":[OSD([sQuery(id+"F2.wireOp",EDGE,"E6"),sQuery(id+"F2.wireOp",EDGE,"E7"),sQuery(id+"F2.wireOp",EDGE,"E8")])],"isStart":false}),makeQuery(id+"F7.opExtrude","SWEPT_FACE",FACE,{"disambiguationData":[OSD([sQuery(id+"F6.wireOp",EDGE,"E30.1")])]})]}),makeQuery(id+"F20.opExtrude","SWEPT_FACE",FACE,{"disambiguationData":[OSD([sQuery(id+"F19.wireOp",EDGE,"E41")])]})]});
            var Q3;
            Q3=makeQuery(id+"F25.boolean.opBoolean","COPY",EDGE,{"derivedFrom":makeQuery(id+"F25.opExtrude","CAP_EDGE",EDGE,{"disambiguationData":[OSD([sQuery(id+"F24.wireOp",EDGE,"746c9b08-4bf7-42f0-bad6-eb23918db56c2.MirrorCS")])],"isStart":true})});
            var Q4;
            Q4=makeQuery(id+"F20.boolean.opBoolean","COPY",EDGE,{"derivedFrom":makeQuery(id+"F20.opExtrude","CAP_EDGE",EDGE,{"disambiguationData":[OSD([sQuery(id+"F19.wireOp",EDGE,"E41")])],"isStart":true})});
            var Q5;
            Q5=makeQuery(id+"F25.boolean.opBoolean","COPY",EDGE,{"derivedFrom":makeQuery(id+"F25.opExtrude","CAP_EDGE",EDGE,{"disambiguationData":[OSD([sQuery(id+"F24.wireOp",EDGE,"lX9O3FEn-HbnI-OlqI-AIzp-qvg3DOlkjrkr")])],"isStart":true})});
            var Q6;
            Q6=makeQuery(id+"F17.boolean.opBoolean","INTERSECT",EDGE,{"derivedFrom":[makeQuery(id+"F1.opExtrude","CAP_FACE",FACE,{"disambiguationData":[OSD([sQuery(id+"F0.wireOp",EDGE,"E0"),sQuery(id+"F0.wireOp",EDGE,"E1"),sQuery(id+"F0.wireOp",EDGE,"E2")])],"isStart":false}),makeQuery(id+"F17.opExtrude","SWEPT_FACE",FACE,{"disambiguationData":[OSD([sQuery(id+"F16.wireOp",EDGE,"E32.1")])]})]});
            var Q7;
            Q7=makeQuery(id+"F17.boolean.opBoolean","INTERSECT",EDGE,{"derivedFrom":[makeQuery(id+"F9.opExtrude","CAP_FACE",FACE,{"disambiguationData":[OSD([sQuery(id+"F8.wireOp",EDGE,"E31.bottom"),sQuery(id+"F8.wireOp",EDGE,"E31.top"),sQuery(id+"F8.wireOp",EDGE,"E31.left"),sQuery(id+"F8.wireOp",EDGE,"E31.right")])],"isStart":false}),makeQuery(id+"F17.opExtrude","SWEPT_FACE",FACE,{"disambiguationData":[OSD([sQuery(id+"F16.wireOp",EDGE,"E33.0")])]})]});
            chamfer(context, id + "F26", {"entities" : qUnion([Q0, Q1, Q2, Q3, Q4, Q5, Q6, Q7]), "width" : .5 * mm, "tangentPropagation" : true});
        }
        {
            var Q0;
            {var subQ0=sQuery(id+"F6.wireOp",EDGE,"E30.1");var subQ1=sQuery(id+"F2.wireOp",EDGE,"E8");var subQ2=sQuery(id+"F2.wireOp",EDGE,"E7");var subQ3=sQuery(id+"F2.wireOp",EDGE,"E6");Q0=makeQuery(id+"F22.boolean.opBoolean","MERGE",FACE,{"derivedFrom":[makeQuery(id+"F7.boolean.opBoolean","MERGE",FACE,{"derivedFrom":[makeQuery(id+"F3.opExtrude","CAP_FACE",FACE,{"disambiguationData":[OSD([subQ3,subQ2,subQ1])],"isStart":false}),makeQuery(id+"F7.opExtrude","SWEPT_FACE",FACE,{"disambiguationData":[OSD([subQ0])]})]}),makeQuery(id+"F22.opExtrude","CAP_FACE",FACE,{"disambiguationData":[OSD([subQ3,subQ2,subQ1,subQ0]),ownerDisambiguation([makeQuery(id+"F22.opExtrude","SWEPT_BODY",BODY,{"disambiguationData":[OSD([sQuery(id+"F21.wireOp",EDGE,"E47.0"),sQuery(id+"F21.wireOp",EDGE,"E48"),sQuery(id+"F21.wireOp",EDGE,"E49"),sQuery(id+"F21.wireOp",EDGE,"E50"),sQuery(id+"F21.wireOp",EDGE,"E51")])]})])],"isStart":false}),makeQuery(id+"F22.opExtrude","CAP_FACE",FACE,{"disambiguationData":[OSD([subQ3,subQ2,subQ1,subQ0]),ownerDisambiguation([makeQuery(id+"F22.opExtrude","SWEPT_BODY",BODY,{"disambiguationData":[OSD([sQuery(id+"F21.wireOp",EDGE,"E52.MirrorCS"),sQuery(id+"F21.wireOp",EDGE,"E53.MirrorCS"),sQuery(id+"F21.wireOp",EDGE,"E54.MirrorCS"),sQuery(id+"F21.wireOp",EDGE,"E55.MirrorCS"),sQuery(id+"F21.wireOp",EDGE,"E56.MirrorCS")])]})])],"isStart":false})]});}
            var sketch = newSketch(context, id + "F27", { "sketchPlane" : qUnion([Q0])});
            skCircle(sketch, "E71", {"center": v(-7, 9) * mm, "radius": 1.99 * mm});
            skCircle(sketch, "E72.MirrorC", {"center": v(7, 9) * mm, "radius": 1.99 * mm});
            skSolve(sketch);
        }
        {
            var Q0;
            Q0 = qSketchRegion(id + "F27", true);
            extrude(context, id + "F28", {"entities" : qUnion([Q0]), "operationType" : NewBodyOperationType.REMOVE, "endBound" : BoundingType.THROUGH_ALL, "oppositeDirection" : true, "depth" : 25 * mm, "offsetDistance" : 25 * mm});
        }
        {
            var Q0;
            Q0=makeQuery(id+"F20.boolean.opBoolean","COPY",EDGE,{"derivedFrom":makeQuery(id+"F20.opExtrude","SWEPT_EDGE",EDGE,{"disambiguationData":[OSD([sQuery(id+"F6.wireOp",EDGE,"E30.3"),sQuery(id+"F19.wireOp",EDGE,"E43"),sQuery(id+"F19.wireOp",EDGE,"E45")])]})});
            var Q1;
            Q1=makeQuery(id+"F20.boolean.opBoolean","COPY",EDGE,{"derivedFrom":makeQuery(id+"F20.opExtrude","SWEPT_EDGE",EDGE,{"disambiguationData":[OSD([sQuery(id+"F6.wireOp",EDGE,"E30.3"),sQuery(id+"F19.wireOp",EDGE,"E44"),sQuery(id+"F19.wireOp",EDGE,"E45")])]})});
            fillet(context, id + "F29", {"entities" : qUnion([Q0, Q1]), "radius" : 2.5 * mm, "tangentPropagation" : true, "allowEdgeOverflow" : false});
        }
    });
